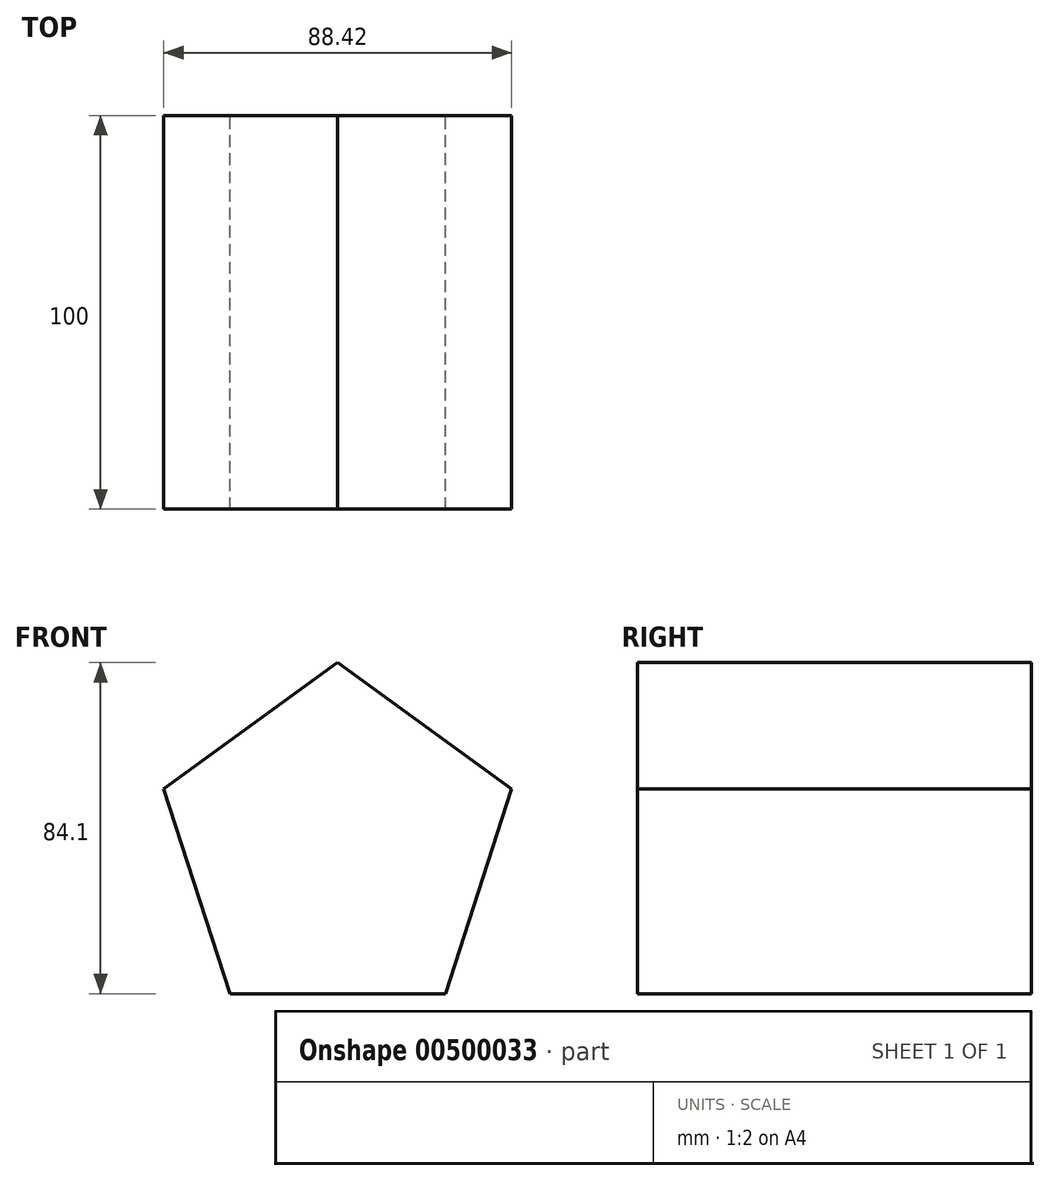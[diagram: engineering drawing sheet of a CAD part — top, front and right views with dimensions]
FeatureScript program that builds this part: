
annotation { "Feature Type Name" : "Feature", "Feature Type Description" : "" }
export const myFeature = defineFeature(function(context is Context, id is Id, definition is map)
    precondition{}
    {
        {
            var Q0;
            Q0=qCreatedBy(makeId("Front.planeOp"),FACE);
            var sketch = newSketch(context, id + "F0", { "sketchPlane" : qUnion([Q0])});
            skCircle(sketch, "E0.cCircle", {"center": v(0, 0) * mm, "radius": 46.5 * mm, "construction": true});
            skLineSegment(sketch, "E0.0", {"start": v(0, 46.5) * mm, "end": v(44.21, 14.37) * mm});
            skLineSegment(sketch, "E0.1", {"start": v(44.21, 14.37) * mm, "end": v(27.33, -37.61) * mm});
            skLineSegment(sketch, "E0.2", {"start": v(27.33, -37.61) * mm, "end": v(-27.33, -37.61) * mm});
            skLineSegment(sketch, "E0.3", {"start": v(-27.33, -37.61) * mm, "end": v(-44.21, 14.37) * mm});
            skLineSegment(sketch, "E0.4", {"start": v(-44.21, 14.37) * mm, "end": v(0, 46.5) * mm});
            skSolve(sketch);
        }
        {
            var Q0;
            Q0 = qSketchRegion(id + "F0", true);
            extrude(context, id + "F1", {"entities" : qUnion([Q0]), "endBound" : BoundingType.SYMMETRIC, "depth" : 100 * mm});
        }
    });
